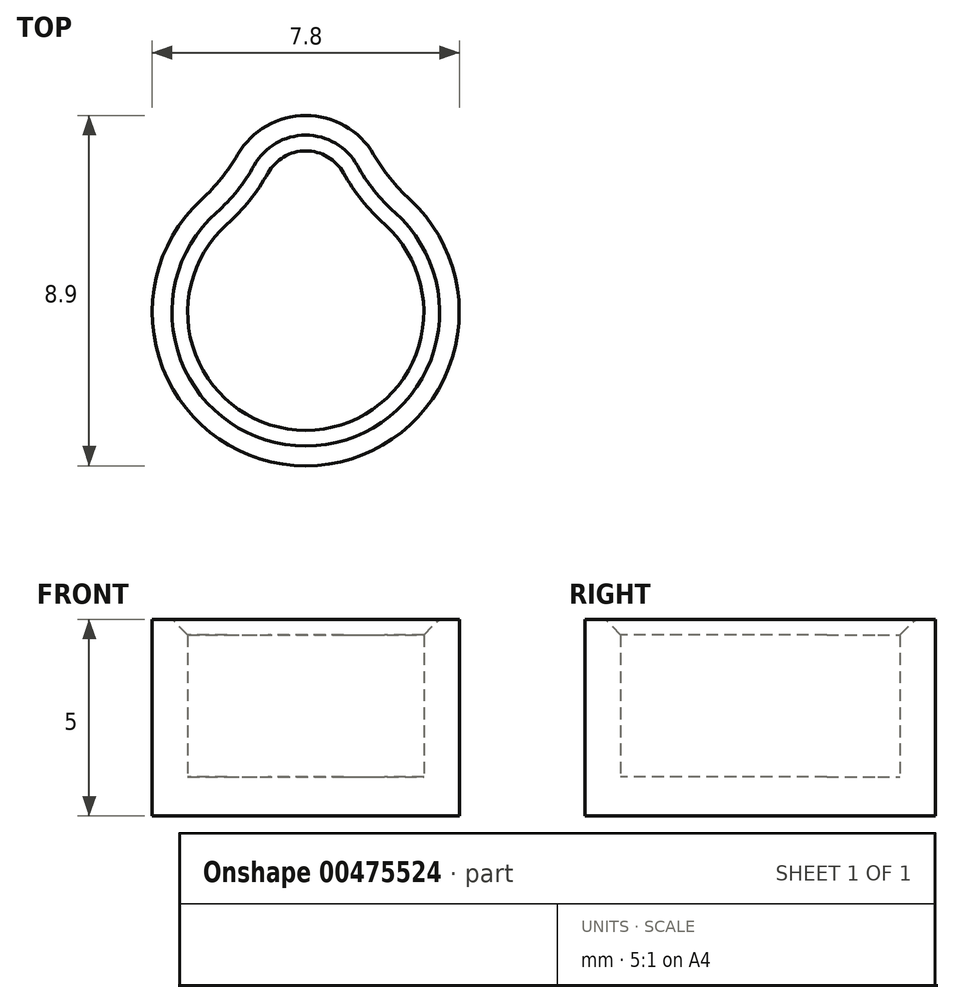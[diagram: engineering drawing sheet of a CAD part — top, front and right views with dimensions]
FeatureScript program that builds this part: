
annotation { "Feature Type Name" : "Feature", "Feature Type Description" : "" }
export const myFeature = defineFeature(function(context is Context, id is Id, definition is map)
    precondition{}
    {
        {
            var Q0;
            Q0=qCreatedBy(makeId("Top.planeOp"),FACE);
            var sketch = newSketch(context, id + "F0", { "sketchPlane" : qUnion([Q0])});
            skArc(sketch, "E0", {"start": v(-2, 2.24) * mm, "mid": v(0, -3) * mm, "end": v(2, 2.24) * mm});
            skArc(sketch, "E1.0", {"start": v(-2.65, 2.86) * mm, "mid": v(0, -3.9) * mm, "end": v(2.65, 2.86) * mm});
            skArc(sketch, "E2", {"start": v(1.73, 4.01) * mm, "mid": v(0, 5) * mm, "end": v(-1.73, 4.01) * mm});
            skArc(sketch, "E3.converted", {"start": v(0.96, 3.53) * mm, "mid": v(0, 4.1) * mm, "end": v(-0.96, 3.53) * mm});
            skPoint(sketch, "E4.visualSharp", {"position": v(-1.08, 2.8) * mm});
            skArc(sketch, "E4.filletArc", {"start": v(-2, 2.24) * mm, "mid": v(-1.43, 2.84) * mm, "end": v(-0.96, 3.53) * mm});
            skPoint(sketch, "E5.visualSharp", {"position": v(1.08, 2.8) * mm});
            skArc(sketch, "E5.filletArc", {"start": v(0.96, 3.53) * mm, "mid": v(1.43, 2.84) * mm, "end": v(2, 2.24) * mm});
            skPoint(sketch, "E6.visualSharp", {"position": v(1.97, 3.37) * mm});
            skArc(sketch, "E6.filletArc", {"start": v(1.73, 4.01) * mm, "mid": v(2.14, 3.4) * mm, "end": v(2.65, 2.86) * mm});
            skPoint(sketch, "E7.visualSharp", {"position": v(-1.97, 3.37) * mm});
            skArc(sketch, "E7.filletArc", {"start": v(-2.65, 2.86) * mm, "mid": v(-2.14, 3.4) * mm, "end": v(-1.73, 4.01) * mm});
            skSolve(sketch);
        }
        {
            var Q0;
            Q0 = qSketchRegion(id + "F0", true);
            extrude(context, id + "F1", {"entities" : qUnion([Q0]), "depth" : 5 * mm});
        }
        {
            var Q0;
            Q0=qCreatedBy(makeId("Top.planeOp"),FACE);
            var sketch = newSketch(context, id + "F2", { "sketchPlane" : qUnion([Q0])});
            skArc(sketch, "E8.0", {"start": v(-2, 2.24) * mm, "mid": v(-1.43, 2.84) * mm, "end": v(-0.96, 3.53) * mm});
            skArc(sketch, "E8.1", {"start": v(0.96, 3.53) * mm, "mid": v(0, 4.1) * mm, "end": v(-0.96, 3.53) * mm});
            skArc(sketch, "E8.2", {"start": v(0.96, 3.53) * mm, "mid": v(1.43, 2.84) * mm, "end": v(2, 2.24) * mm});
            skArc(sketch, "E8.3", {"start": v(-2, 2.24) * mm, "mid": v(0, -3) * mm, "end": v(2, 2.24) * mm});
            skSolve(sketch);
        }
        {
            var Q0;
            Q0 = qSketchRegion(id + "F2", true);
            extrude(context, id + "F3", {"entities" : qUnion([Q0]), "operationType" : NewBodyOperationType.ADD, "depth" : 1 * mm});
        }
        {
            var Q0;
            Q0=makeQuery(id+"F1.opExtrude","CAP_EDGE",EDGE,{"disambiguationData":[OSD([sQuery(id+"F0.wireOp",EDGE,"E0")])],"isStart":false});
            chamfer(context, id + "F4", {"entities" : qUnion([Q0]), "width" : 0.4 * mm, "tangentPropagation" : true});
        }
    });
